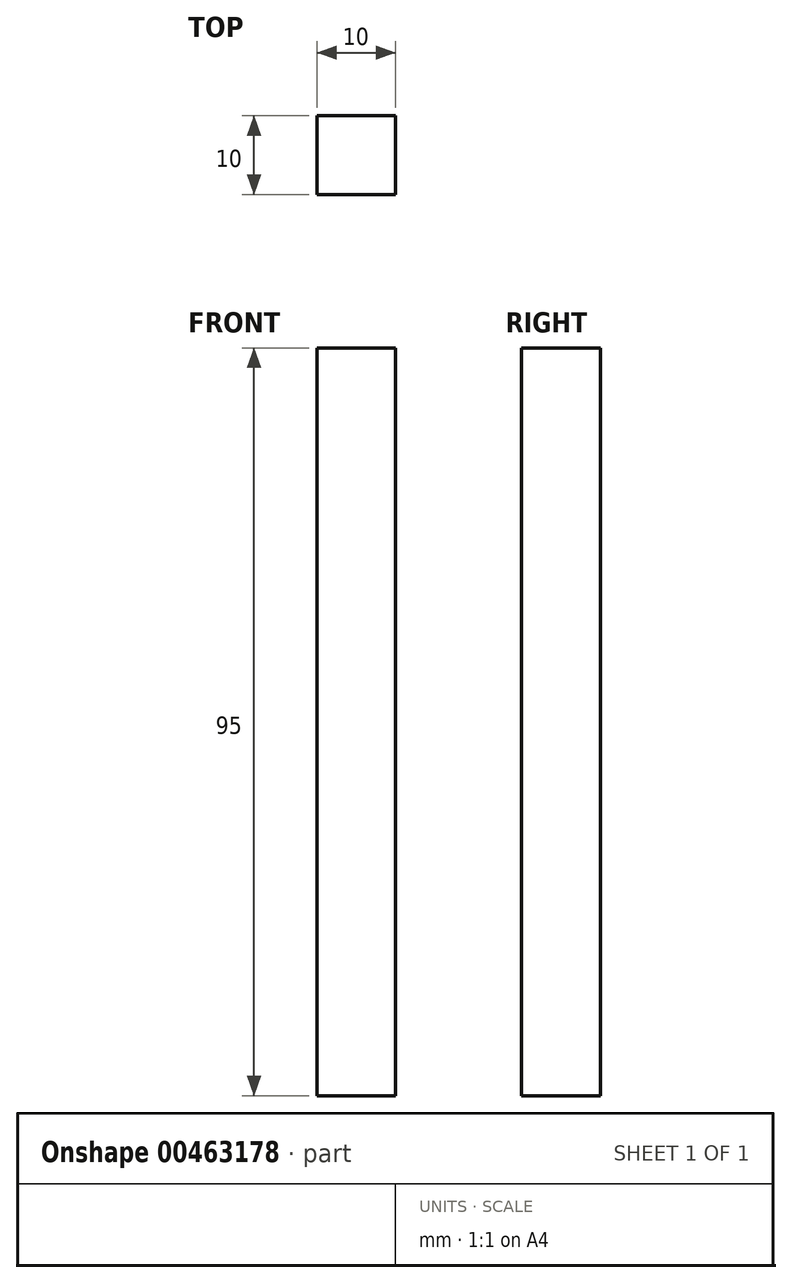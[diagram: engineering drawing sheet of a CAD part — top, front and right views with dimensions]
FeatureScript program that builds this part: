
annotation { "Feature Type Name" : "Feature", "Feature Type Description" : "" }
export const myFeature = defineFeature(function(context is Context, id is Id, definition is map)
    precondition{}
    {
        {
            var Q0;
            Q0=qCreatedBy(makeId("Front.planeOp"),FACE);
            var sketch = newSketch(context, id + "F0", { "sketchPlane" : qUnion([Q0])});
            skLineSegment(sketch, "E0.bottom", {"start": v(10, 95) * mm, "end": v(0, 95) * mm});
            skLineSegment(sketch, "E0.top", {"start": v(10, 0) * mm, "end": v(0, 0) * mm});
            skLineSegment(sketch, "E0.left", {"start": v(10, 95) * mm, "end": v(10, 0) * mm});
            skLineSegment(sketch, "E0.right", {"start": v(0, 95) * mm, "end": v(0, 0) * mm});
            skSolve(sketch);
        }
        {
            var Q0;
            Q0=makeQuery(id+"F0.imprint","IMPRINT",FACE,{"disambiguationData":[TD([[makeQuery(id+"F0.imprint","IMPRINT",EDGE,{"derivedFrom":sQuery(id+"F0.wireOp",EDGE,"E0.bottom")}),1.0]])]});
            extrude(context, id + "F1", {"entities" : qUnion([Q0]), "depth" : 10 * mm});
        }
    });
